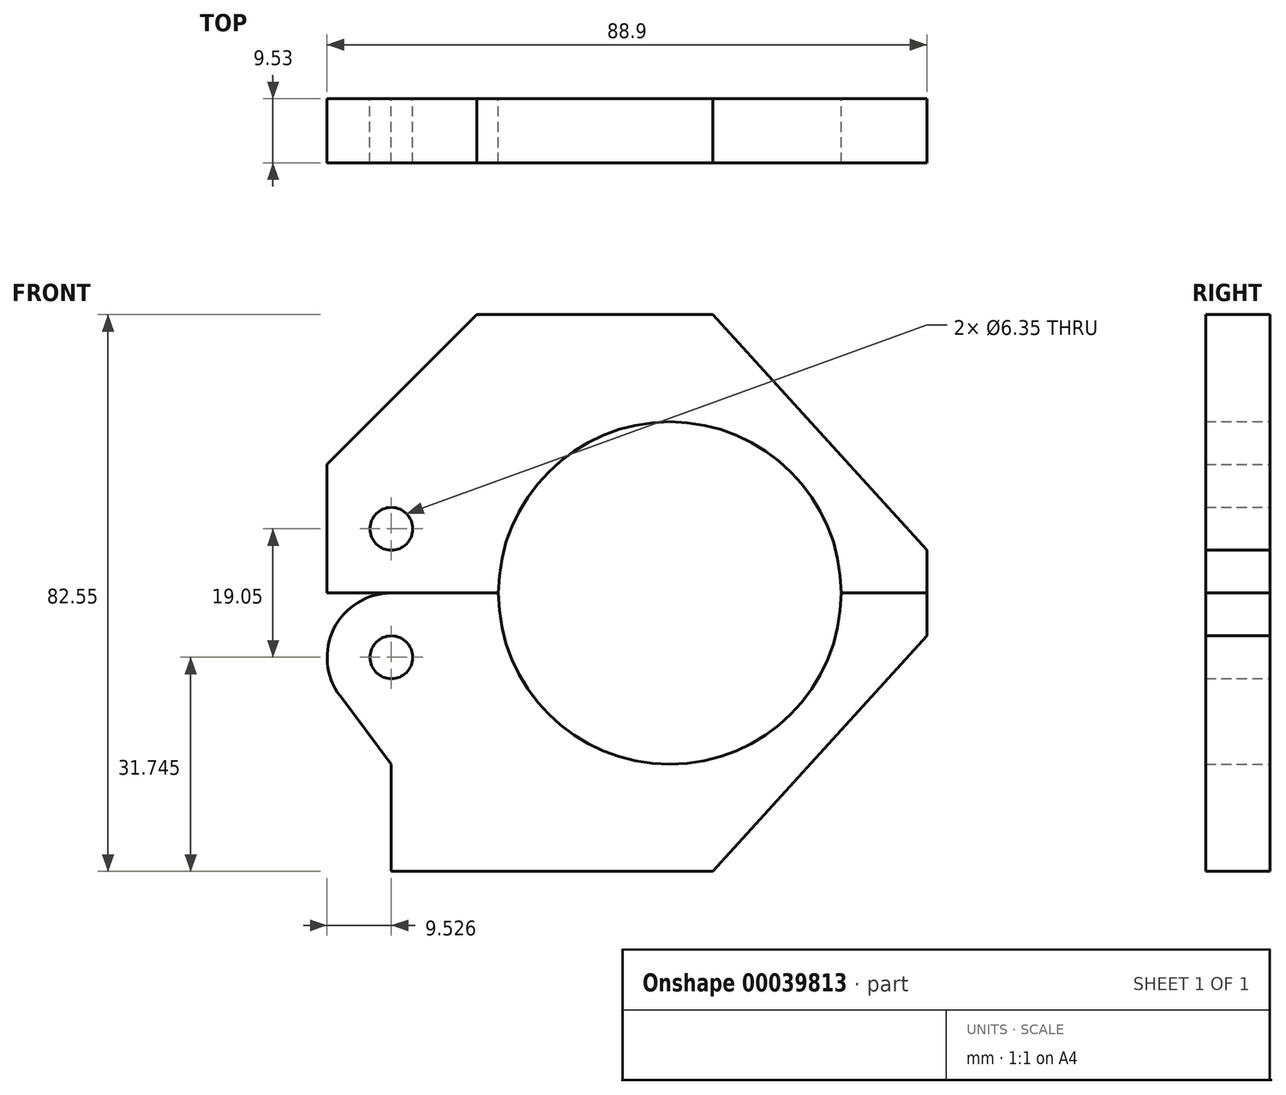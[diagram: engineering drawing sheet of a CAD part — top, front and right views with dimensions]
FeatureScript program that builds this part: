
annotation { "Feature Type Name" : "Feature", "Feature Type Description" : "" }
export const myFeature = defineFeature(function(context is Context, id is Id, definition is map)
    precondition{}
    {
        {
            var Q0;
            Q0=qCreatedBy(makeId("Front.planeOp"),FACE);
            var sketch = newSketch(context, id + "F0", { "sketchPlane" : qUnion([Q0])});
            skLineSegment(sketch, "E0.bottom", {"start": v(-56.28, -33.86) * mm, "end": v(-8.66, -33.86) * mm});
            skLineSegment(sketch, "E0.top", {"start": v(-43.58, 48.69) * mm, "end": v(-8.66, 48.69) * mm});
            skLineSegment(sketch, "E0.left", {"start": v(-65.8, 7.41) * mm, "end": v(-65.8, 26.46) * mm});
            skLineSegment(sketch, "E0.right", {"start": v(23.1, 1.06) * mm, "end": v(23.1, 13.76) * mm});
            skLineSegment(sketch, "E1", {"start": v(-65.8, 7.41) * mm, "end": v(23.1, 7.41) * mm});
            skCircle(sketch, "E2", {"center": v(-15, 7.41) * mm, "radius": 25.4 * mm});
            skLineSegment(sketch, "E3", {"start": v(23.1, 13.76) * mm, "end": v(-8.66, 48.69) * mm});
            skLineSegment(sketch, "E4.MirrorCS", {"start": v(23.1, 1.06) * mm, "end": v(-8.66, -33.86) * mm});
            skLineSegment(sketch, "E5", {"start": v(-43.58, 48.69) * mm, "end": v(-65.8, 26.46) * mm});
            skCircle(sketch, "E6", {"center": v(-56.28, 16.94) * mm, "radius": 3.18 * mm});
            skCircle(sketch, "E7.MirrorC", {"center": v(-56.28, -2.11) * mm, "radius": 3.18 * mm});
            skLineSegment(sketch, "E8", {"start": v(-56.28, -33.86) * mm, "end": v(-56.28, -17.99) * mm});
            skArc(sketch, "E9", {"start": v(-56.28, 7.41) * mm, "mid": v(-64.8, 2.15) * mm, "end": v(-63.9, -7.83) * mm});
            skLineSegment(sketch, "E10", {"start": v(-56.28, -17.99) * mm, "end": v(-63.9, -7.83) * mm});
            skPoint(sketch, "E11.orphan", {"position": v(23.1, 48.69) * mm});
            skPoint(sketch, "E12.orphan", {"position": v(23.1, -33.86) * mm});
            skPoint(sketch, "E13.orphan", {"position": v(-65.8, -33.86) * mm});
            skPoint(sketch, "E14.orphan", {"position": v(-65.8, 48.69) * mm});
            skSolve(sketch);
        }
        {
            var Q0;
            Q0=makeQuery(id+"F0.imprint","IMPRINT",FACE,{"disambiguationData":[TD([[makeQuery(id+"F0.imprint","IMPRINT",EDGE,{"derivedFrom":sQuery(id+"F0.wireOp",EDGE,"E0.top")}),-1.0]])]});
            extrude(context, id + "F1", {"entities" : qUnion([Q0]), "depth" : 9.52 * mm});
        }
        {
            var Q0;
            Q0=makeQuery(id+"F0.imprint","IMPRINT",FACE,{"disambiguationData":[TD([[makeQuery(id+"F0.imprint","IMPRINT",EDGE,{"derivedFrom":sQuery(id+"F0.wireOp",EDGE,"E0.bottom")}),1.0]])]});
            extrude(context, id + "F2", {"entities" : qUnion([Q0]), "depth" : 9.52 * mm});
        }
    });
